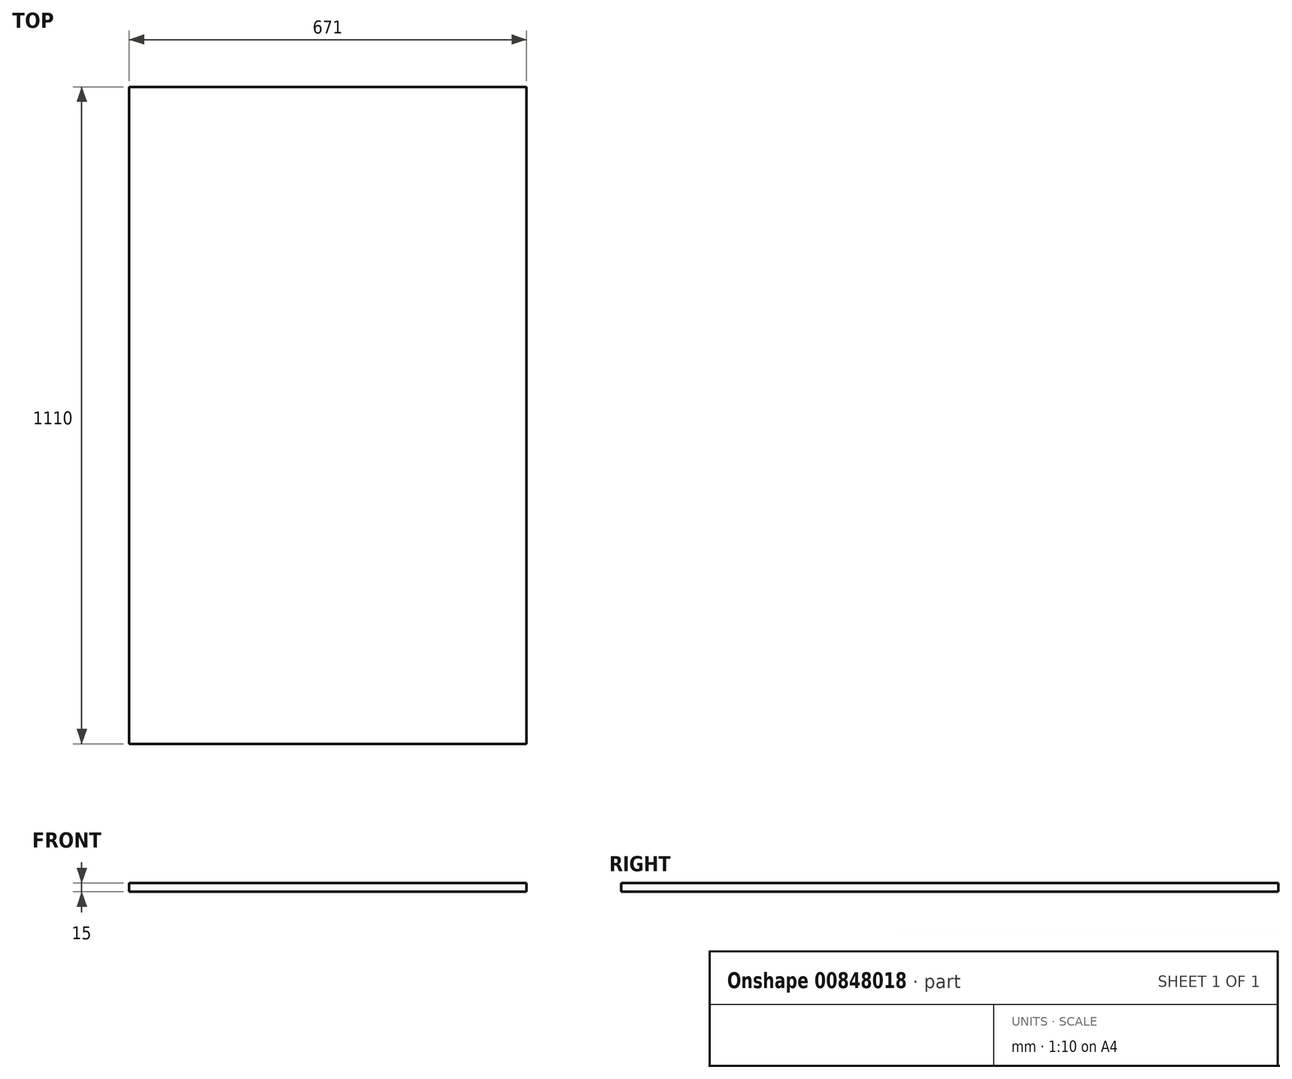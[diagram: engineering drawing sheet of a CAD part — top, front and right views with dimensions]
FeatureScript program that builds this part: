
annotation { "Feature Type Name" : "Feature", "Feature Type Description" : "" }
export const myFeature = defineFeature(function(context is Context, id is Id, definition is map)
    precondition{}
    {
        {
            var Q0;
            Q0=qCreatedBy(makeId("Top.planeOp"),FACE);
            var sketch = newSketch(context, id + "F0", { "sketchPlane" : qUnion([Q0])});
            skLineSegment(sketch, "E0.bottom", {"start": v(-335.5, -555) * mm, "end": v(335.5, -555) * mm});
            skLineSegment(sketch, "E0.top", {"start": v(-335.5, 555) * mm, "end": v(335.5, 555) * mm});
            skLineSegment(sketch, "E0.left", {"start": v(-335.5, -555) * mm, "end": v(-335.5, 555) * mm});
            skLineSegment(sketch, "E0.right", {"start": v(335.5, -555) * mm, "end": v(335.5, 555) * mm});
            skSolve(sketch);
        }
        {
            var Q0;
            Q0=makeQuery(id+"F0.imprint","IMPRINT",FACE,{"disambiguationData":[TD([[makeQuery(id+"F0.imprint","IMPRINT",EDGE,{"derivedFrom":sQuery(id+"F0.wireOp",EDGE,"E0.bottom")}),1.0]])]});
            extrude(context, id + "F1", {"entities" : qUnion([Q0]), "depth" : 15 * mm, "offsetDistance" : 25 * mm});
        }
    });
